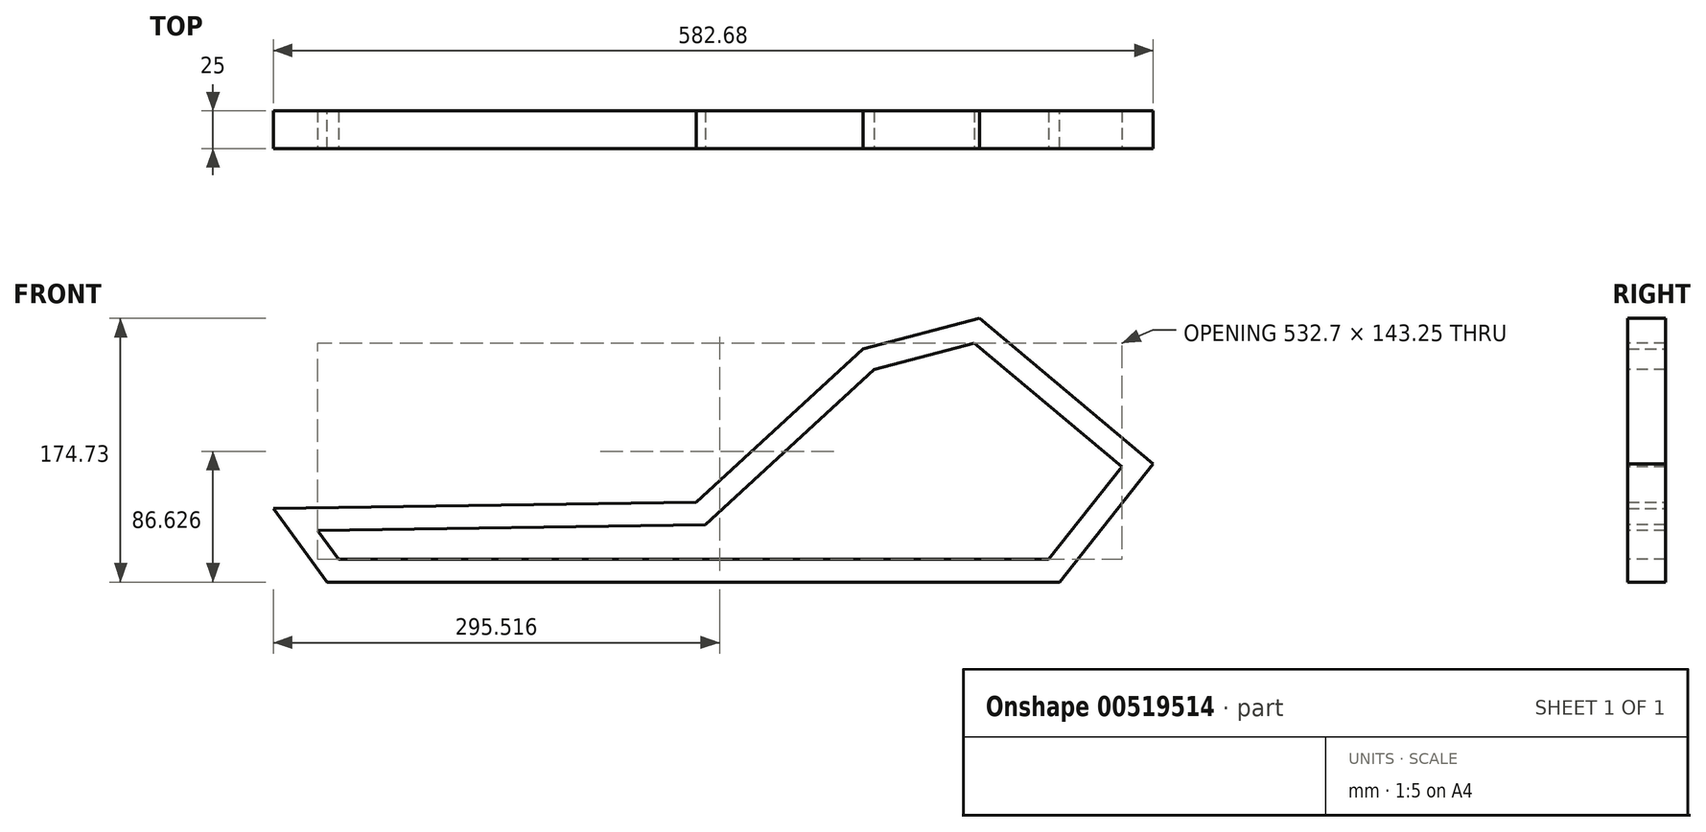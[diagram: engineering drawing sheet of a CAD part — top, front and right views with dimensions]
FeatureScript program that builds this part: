
annotation { "Feature Type Name" : "Feature", "Feature Type Description" : "" }
export const myFeature = defineFeature(function(context is Context, id is Id, definition is map)
    precondition{}
    {
        {
            var Q0;
            Q0=qCreatedBy(makeId("Front.planeOp"),FACE);
            var sketch = newSketch(context, id + "F0", { "sketchPlane" : qUnion([Q0])});
            skLineSegment(sketch, "E0", {"start": v(0, 0) * mm, "end": v(235, 0) * mm});
            skLineSegment(sketch, "E1", {"start": v(235, 0) * mm, "end": v(297.1, 78.39) * mm});
            skLineSegment(sketch, "E2", {"start": v(297.1, 78.39) * mm, "end": v(182.12, 174.73) * mm});
            skLineSegment(sketch, "E3", {"start": v(182.12, 174.73) * mm, "end": v(104.75, 154.39) * mm});
            skLineSegment(sketch, "E4", {"start": v(104.75, 154.39) * mm, "end": v(-5.62, 52.81) * mm});
            skLineSegment(sketch, "E5", {"start": v(-5.62, 52.81) * mm, "end": v(-285.6, 48.92) * mm});
            skLineSegment(sketch, "E6", {"start": v(-285.6, 48.92) * mm, "end": v(-250, 0) * mm});
            skLineSegment(sketch, "E7", {"start": v(-250, 0) * mm, "end": v(0, 0) * mm});
            skSolve(sketch);
        }
        {
            var Q0;
            Q0 = qSketchRegion(id + "F0", true);
            extrude(context, id + "F1", {"entities" : qUnion([Q0]), "depth" : 25 * mm, "offsetDistance" : 25 * mm});
        }
        {
            var Q0;
            Q0=makeQuery(id+"F1.opExtrude","CAP_FACE",FACE,{"disambiguationData":[OSD([sQuery(id+"F0.wireOp",EDGE,"E0"),sQuery(id+"F0.wireOp",EDGE,"E1"),sQuery(id+"F0.wireOp",EDGE,"E2"),sQuery(id+"F0.wireOp",EDGE,"E3"),sQuery(id+"F0.wireOp",EDGE,"E4"),sQuery(id+"F0.wireOp",EDGE,"E5"),sQuery(id+"F0.wireOp",EDGE,"E6"),sQuery(id+"F0.wireOp",EDGE,"E7")])],"isStart":false});
            var sketch = newSketch(context, id + "F2", { "sketchPlane" : qUnion([Q0])});
            skLineSegment(sketch, "E8.0", {"start": v(112.17, 140.83) * mm, "end": v(0.32, 37.9) * mm});
            skLineSegment(sketch, "E9.0", {"start": v(178.44, 158.25) * mm, "end": v(112.17, 140.83) * mm});
            skLineSegment(sketch, "E10.0", {"start": v(276.27, 76.26) * mm, "end": v(178.44, 158.25) * mm});
            skLineSegment(sketch, "E11.0", {"start": v(227.75, 15) * mm, "end": v(276.27, 76.26) * mm});
            skLineSegment(sketch, "E12.0", {"start": v(-242.36, 15) * mm, "end": v(227.75, 15) * mm});
            skLineSegment(sketch, "E13.0", {"start": v(-256.42, 34.33) * mm, "end": v(-242.36, 15) * mm});
            skLineSegment(sketch, "E14.0", {"start": v(0.32, 37.9) * mm, "end": v(-256.42, 34.33) * mm});
            skSolve(sketch);
        }
        {
            var Q0;
            Q0=makeQuery(id+"F2.imprint","IMPRINT",FACE,{"disambiguationData":[TD([[makeQuery(id+"F2.imprint","IMPRINT",EDGE,{"derivedFrom":sQuery(id+"F2.wireOp",EDGE,"E8.0")}),1.0]])]});
            extrude(context, id + "F3", {"entities" : qUnion([Q0]), "operationType" : NewBodyOperationType.REMOVE, "oppositeDirection" : true, "depth" : 25 * mm, "offsetDistance" : 25 * mm});
        }
    });
